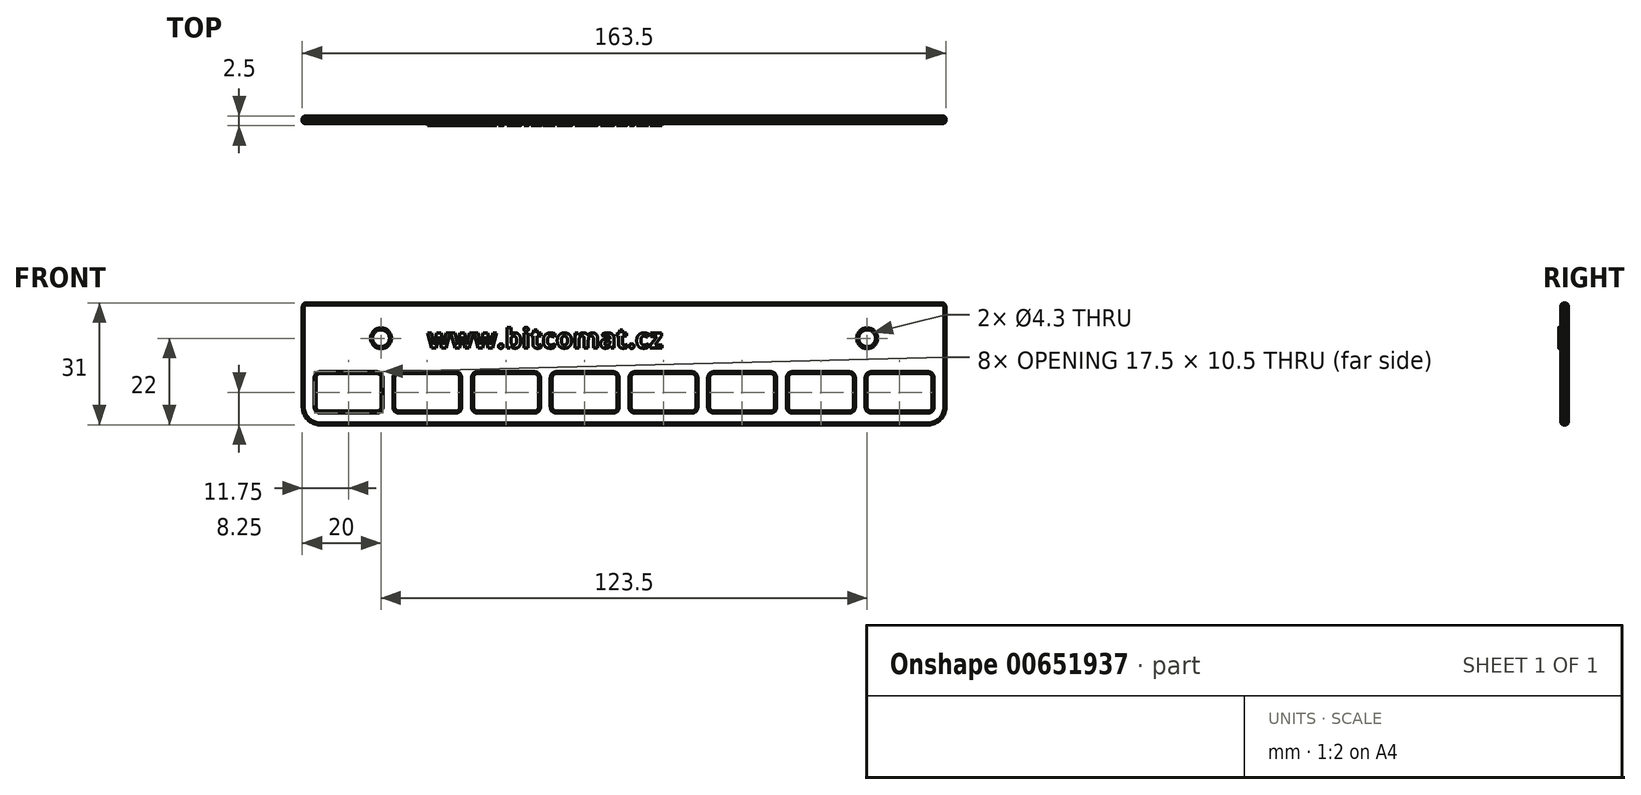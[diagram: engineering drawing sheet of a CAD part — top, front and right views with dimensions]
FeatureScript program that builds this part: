
annotation { "Feature Type Name" : "Feature", "Feature Type Description" : "" }
export const myFeature = defineFeature(function(context is Context, id is Id, definition is map)
    precondition{}
    {
        {
            var Q0;
            Q0=qCreatedBy(makeId("Front.planeOp"),FACE);
            var sketch = newSketch(context, id + "F0", { "sketchPlane" : qUnion([Q0])});
            skLineSegment(sketch, "E0", {"start": v(0, 0) * mm, "end": v(0, 31) * mm});
            skLineSegment(sketch, "E1", {"start": v(0, 31) * mm, "end": v(163.5, 31) * mm});
            skLineSegment(sketch, "E2", {"start": v(163.5, 31) * mm, "end": v(163.5, 0) * mm});
            skCircle(sketch, "E3", {"center": v(20, 22) * mm, "radius": 2.15 * mm});
            skCircle(sketch, "E4", {"center": v(143.5, 22) * mm, "radius": 2.15 * mm});
            skLineSegment(sketch, "E5", {"start": v(0, 0) * mm, "end": v(163.5, 0) * mm});
            skLineSegment(sketch, "E6.bottom", {"start": v(3.5, 13) * mm, "end": v(20, 13) * mm});
            skLineSegment(sketch, "E6.top", {"start": v(3.5, 3.5) * mm, "end": v(20, 3.5) * mm});
            skLineSegment(sketch, "E6.left", {"start": v(3.5, 13) * mm, "end": v(3.5, 3.5) * mm});
            skLineSegment(sketch, "E6.right", {"start": v(20, 13) * mm, "end": v(20, 3.5) * mm});
            skLineSegment(sketch, "E7.bottom", {"start": v(23.5, 13) * mm, "end": v(40, 13) * mm});
            skLineSegment(sketch, "E7.top", {"start": v(23.5, 3.5) * mm, "end": v(40, 3.5) * mm});
            skLineSegment(sketch, "E7.left", {"start": v(23.5, 13) * mm, "end": v(23.5, 3.5) * mm});
            skLineSegment(sketch, "E7.right", {"start": v(40, 13) * mm, "end": v(40, 3.5) * mm});
            skLineSegment(sketch, "E8.bottom", {"start": v(43.5, 13) * mm, "end": v(60, 13) * mm});
            skLineSegment(sketch, "E8.top", {"start": v(43.5, 3.5) * mm, "end": v(60, 3.5) * mm});
            skLineSegment(sketch, "E8.left", {"start": v(43.5, 13) * mm, "end": v(43.5, 3.5) * mm});
            skLineSegment(sketch, "E8.right", {"start": v(60, 13) * mm, "end": v(60, 3.5) * mm});
            skLineSegment(sketch, "E9.bottom", {"start": v(63.5, 13) * mm, "end": v(80, 13) * mm});
            skLineSegment(sketch, "E9.top", {"start": v(63.5, 3.5) * mm, "end": v(80, 3.5) * mm});
            skLineSegment(sketch, "E9.left", {"start": v(63.5, 13) * mm, "end": v(63.5, 3.5) * mm});
            skLineSegment(sketch, "E9.right", {"start": v(80, 13) * mm, "end": v(80, 3.5) * mm});
            skLineSegment(sketch, "E10.bottom", {"start": v(83.5, 13) * mm, "end": v(100, 13) * mm});
            skLineSegment(sketch, "E10.top", {"start": v(83.5, 3.5) * mm, "end": v(100, 3.5) * mm});
            skLineSegment(sketch, "E10.left", {"start": v(83.5, 13) * mm, "end": v(83.5, 3.5) * mm});
            skLineSegment(sketch, "E10.right", {"start": v(100, 13) * mm, "end": v(100, 3.5) * mm});
            skLineSegment(sketch, "E11.bottom", {"start": v(103.5, 13) * mm, "end": v(120, 13) * mm});
            skLineSegment(sketch, "E11.top", {"start": v(103.5, 3.5) * mm, "end": v(120, 3.5) * mm});
            skLineSegment(sketch, "E11.left", {"start": v(103.5, 13) * mm, "end": v(103.5, 3.5) * mm});
            skLineSegment(sketch, "E11.right", {"start": v(120, 13) * mm, "end": v(120, 3.5) * mm});
            skLineSegment(sketch, "E12.bottom", {"start": v(123.5, 13) * mm, "end": v(140, 13) * mm});
            skLineSegment(sketch, "E12.top", {"start": v(123.5, 3.5) * mm, "end": v(140, 3.5) * mm});
            skLineSegment(sketch, "E12.left", {"start": v(123.5, 13) * mm, "end": v(123.5, 3.5) * mm});
            skLineSegment(sketch, "E12.right", {"start": v(140, 13) * mm, "end": v(140, 3.5) * mm});
            skLineSegment(sketch, "E13.bottom", {"start": v(143.5, 13) * mm, "end": v(160, 13) * mm});
            skLineSegment(sketch, "E13.top", {"start": v(143.5, 3.5) * mm, "end": v(160, 3.5) * mm});
            skLineSegment(sketch, "E13.left", {"start": v(143.5, 13) * mm, "end": v(143.5, 3.5) * mm});
            skLineSegment(sketch, "E13.right", {"start": v(160, 13) * mm, "end": v(160, 3.5) * mm});
            skSolve(sketch);
        }
        {
            var Q0;
            Q0 = qSketchRegion(id + "F0", true);
            extrude(context, id + "F1", {"entities" : qUnion([Q0]), "depth" : 2 * mm, "offsetDistance" : 25 * mm});
        }
        {
            var Q0;
            Q0=makeQuery(id+"F1.opExtrude","SWEPT_EDGE",EDGE,{"disambiguationData":[OSD([sQuery(id+"F0.wireOp",EDGE,"8d9dad82-93ce-4f2d-81da-381c7b047625.trimOffspring"),sQuery(id+"F0.wireOp",EDGE,"Q4MqpzYb-z3Ok-xj9e-ZRvY-jZGfUojLIxkK")])]});
            var Q1;
            Q1=makeQuery(id+"F1.opExtrude","SWEPT_EDGE",EDGE,{"disambiguationData":[OSD([sQuery(id+"F0.wireOp",EDGE,"314859cf-d446-4f25-8f78-4489ed11554f.trimOffspring"),sQuery(id+"F0.wireOp",EDGE,"7d0YZfYc-MtNi-HNez-lG2K-TYVgYgpoHqIJ")])]});
            var Q2;
            Q2=makeQuery(id+"F1.opExtrude","SWEPT_EDGE",EDGE,{"disambiguationData":[OSD([sQuery(id+"F0.wireOp",EDGE,"4a782518-a8ca-412a-b276-fc9fadfd2a7f.trimOffspring"),sQuery(id+"F0.wireOp",EDGE,"5vtNxTYR-MAFZ-9926-d2hc-BvAu6AeZHcsb")])]});
            var Q3;
            Q3=makeQuery(id+"F1.opExtrude","SWEPT_EDGE",EDGE,{"disambiguationData":[OSD([sQuery(id+"F0.wireOp",EDGE,"aee5cead-98e0-4757-9163-f8d7b24aee3c.trimOffspring"),sQuery(id+"F0.wireOp",EDGE,"1HIB1zMs-rl4G-Qikl-t2Sc-eNzFZ2GBNpQB")])]});
            var Q4;
            Q4=makeQuery(id+"F1.opExtrude","SWEPT_EDGE",EDGE,{"disambiguationData":[OSD([sQuery(id+"F0.wireOp",EDGE,"952a6334-aa4c-4368-9368-879805710147.trimOffspring"),sQuery(id+"F0.wireOp",EDGE,"39W3pprf-JPW6-z08R-VL7n-OxTiLGvcOl4Z")])]});
            var Q5;
            Q5=makeQuery(id+"F1.opExtrude","SWEPT_EDGE",EDGE,{"disambiguationData":[OSD([sQuery(id+"F0.wireOp",EDGE,"TwgcRK7u-zNJq-IuH6-kE6Y-Pdj6bc34kcyJ"),sQuery(id+"F0.wireOp",EDGE,"NbZKl04f-24VF-Ro1G-Pxu3-JmUhMLliUNzg")])]});
            var Q6;
            Q6=makeQuery(id+"F1.opExtrude","SWEPT_EDGE",EDGE,{"disambiguationData":[OSD([sQuery(id+"F0.wireOp",EDGE,"8d9dad82-93ce-4f2d-81da-381c7b047625.trimOffspring"),sQuery(id+"F0.wireOp",EDGE,"SUHKJSzE-OJzO-pzQp-ywUD-TkapwmwD6V0m")])]});
            var Q7;
            Q7=makeQuery(id+"F1.opExtrude","SWEPT_EDGE",EDGE,{"disambiguationData":[OSD([sQuery(id+"F0.wireOp",EDGE,"7137db87-9400-4fe6-be01-630d94328871.trimOffspring"),sQuery(id+"F0.wireOp",EDGE,"MW19rWYv-jTzx-EUmW-Wu64-N2ipS1HRE4QS")])]});
            var Q8;
            Q8=makeQuery(id+"F1.opExtrude","SWEPT_EDGE",EDGE,{"disambiguationData":[OSD([sQuery(id+"F0.wireOp",EDGE,"314859cf-d446-4f25-8f78-4489ed11554f.trimOffspring"),sQuery(id+"F0.wireOp",EDGE,"OjDirCAP-vRV8-dHmh-1vQw-u1C2cGEMCSFC")])]});
            var Q9;
            Q9=makeQuery(id+"F1.opExtrude","SWEPT_EDGE",EDGE,{"disambiguationData":[OSD([sQuery(id+"F0.wireOp",EDGE,"4a782518-a8ca-412a-b276-fc9fadfd2a7f.trimOffspring"),sQuery(id+"F0.wireOp",EDGE,"MDnvUn5u-0YRr-R42K-GIOI-WnT9jtSQHMXQ")])]});
            var Q10;
            Q10=makeQuery(id+"F1.opExtrude","SWEPT_EDGE",EDGE,{"disambiguationData":[OSD([sQuery(id+"F0.wireOp",EDGE,"aee5cead-98e0-4757-9163-f8d7b24aee3c.trimOffspring"),sQuery(id+"F0.wireOp",EDGE,"P9qTeayO-fJTB-ogTq-NOMs-bO8yJh6IIpOu")])]});
            var Q11;
            Q11=makeQuery(id+"F1.opExtrude","SWEPT_EDGE",EDGE,{"disambiguationData":[OSD([sQuery(id+"F0.wireOp",EDGE,"E0"),sQuery(id+"F0.wireOp",EDGE,"E1")])]});
            var Q12;
            Q12=makeQuery(id+"F1.opExtrude","SWEPT_EDGE",EDGE,{"disambiguationData":[OSD([sQuery(id+"F0.wireOp",EDGE,"E1"),sQuery(id+"F0.wireOp",EDGE,"E2")])]});
            var Q13;
            Q13=makeQuery(id+"F1.opExtrude","SWEPT_EDGE",EDGE,{"disambiguationData":[OSD([sQuery(id+"F0.wireOp",EDGE,"952a6334-aa4c-4368-9368-879805710147.trimOffspring"),sQuery(id+"F0.wireOp",EDGE,"CVMrosdh-o8LT-Kh2A-sdVF-YHnpHe9g5ULG")])]});
            fillet(context, id + "F2", {"entities" : qUnion([Q0, Q1, Q2, Q3, Q4, Q5, Q6, Q7, Q8, Q9, Q10, Q11, Q12, Q13]), "radius" : 1 * mm, "tangentPropagation" : true, "allowEdgeOverflow" : false});
        }
        {
            var Q0;
            Q0=makeQuery(id+"F1.opExtrude","SWEPT_EDGE",EDGE,{"disambiguationData":[OSD([sQuery(id+"F0.wireOp",EDGE,"hVktsJ5d-FybM-sNTf-hAeP-5I45lPSxXoCe"),sQuery(id+"F0.wireOp",EDGE,"Q4MqpzYb-z3Ok-xj9e-ZRvY-jZGfUojLIxkK")])]});
            var Q1;
            Q1=makeQuery(id+"F1.opExtrude","SWEPT_EDGE",EDGE,{"disambiguationData":[OSD([sQuery(id+"F0.wireOp",EDGE,"JEd7AicR-trPV-dsle-exch-AMzUto0O4eAY"),sQuery(id+"F0.wireOp",EDGE,"7d0YZfYc-MtNi-HNez-lG2K-TYVgYgpoHqIJ")])]});
            var Q2;
            Q2=makeQuery(id+"F1.opExtrude","SWEPT_EDGE",EDGE,{"disambiguationData":[OSD([sQuery(id+"F0.wireOp",EDGE,"pn5ojUSX-ob2q-A8bu-eBAn-f9iVDgr16dR8"),sQuery(id+"F0.wireOp",EDGE,"5vtNxTYR-MAFZ-9926-d2hc-BvAu6AeZHcsb")])]});
            var Q3;
            Q3=makeQuery(id+"F1.opExtrude","SWEPT_EDGE",EDGE,{"disambiguationData":[OSD([sQuery(id+"F0.wireOp",EDGE,"OjDirCAP-vRV8-dHmh-1vQw-u1C2cGEMCSFC"),sQuery(id+"F0.wireOp",EDGE,"pn5ojUSX-ob2q-A8bu-eBAn-f9iVDgr16dR8")])]});
            var Q4;
            Q4=makeQuery(id+"F1.opExtrude","SWEPT_EDGE",EDGE,{"disambiguationData":[OSD([sQuery(id+"F0.wireOp",EDGE,"SUHKJSzE-OJzO-pzQp-ywUD-TkapwmwD6V0m"),sQuery(id+"F0.wireOp",EDGE,"JEd7AicR-trPV-dsle-exch-AMzUto0O4eAY")])]});
            var Q5;
            Q5=makeQuery(id+"F1.opExtrude","SWEPT_EDGE",EDGE,{"disambiguationData":[OSD([sQuery(id+"F0.wireOp",EDGE,"MDnvUn5u-0YRr-R42K-GIOI-WnT9jtSQHMXQ"),sQuery(id+"F0.wireOp",EDGE,"S5mCw68c-sqde-8qUc-JXXg-RKrNQSxQ3Wiu")])]});
            var Q6;
            Q6=makeQuery(id+"F1.opExtrude","SWEPT_EDGE",EDGE,{"disambiguationData":[OSD([sQuery(id+"F0.wireOp",EDGE,"P9qTeayO-fJTB-ogTq-NOMs-bO8yJh6IIpOu"),sQuery(id+"F0.wireOp",EDGE,"FKDOqHEf-IVW9-28Ru-xmGw-znab7f26yI2c")])]});
            var Q7;
            Q7=makeQuery(id+"F1.opExtrude","SWEPT_EDGE",EDGE,{"disambiguationData":[OSD([sQuery(id+"F0.wireOp",EDGE,"S5mCw68c-sqde-8qUc-JXXg-RKrNQSxQ3Wiu"),sQuery(id+"F0.wireOp",EDGE,"1HIB1zMs-rl4G-Qikl-t2Sc-eNzFZ2GBNpQB")])]});
            var Q8;
            Q8=makeQuery(id+"F1.opExtrude","SWEPT_EDGE",EDGE,{"disambiguationData":[OSD([sQuery(id+"F0.wireOp",EDGE,"FKDOqHEf-IVW9-28Ru-xmGw-znab7f26yI2c"),sQuery(id+"F0.wireOp",EDGE,"39W3pprf-JPW6-z08R-VL7n-OxTiLGvcOl4Z")])]});
            var Q9;
            Q9=makeQuery(id+"F1.opExtrude","SWEPT_EDGE",EDGE,{"disambiguationData":[OSD([sQuery(id+"F0.wireOp",EDGE,"v1fHItDr-QFj1-3yH0-OkLM-ghUJiiQzrCXv"),sQuery(id+"F0.wireOp",EDGE,"NbZKl04f-24VF-Ro1G-Pxu3-JmUhMLliUNzg")])]});
            var Q10;
            Q10=makeQuery(id+"F1.opExtrude","SWEPT_EDGE",EDGE,{"disambiguationData":[OSD([sQuery(id+"F0.wireOp",EDGE,"CVMrosdh-o8LT-Kh2A-sdVF-YHnpHe9g5ULG"),sQuery(id+"F0.wireOp",EDGE,"v1fHItDr-QFj1-3yH0-OkLM-ghUJiiQzrCXv")])]});
            var Q11;
            Q11=makeQuery(id+"F1.opExtrude","SWEPT_EDGE",EDGE,{"disambiguationData":[OSD([sQuery(id+"F0.wireOp",EDGE,"E2"),sQuery(id+"F0.wireOp",EDGE,"TwgcRK7u-zNJq-IuH6-kE6Y-Pdj6bc34kcyJ")])]});
            var Q12;
            Q12=makeQuery(id+"F1.opExtrude","SWEPT_EDGE",EDGE,{"disambiguationData":[OSD([sQuery(id+"F0.wireOp",EDGE,"E0"),sQuery(id+"F0.wireOp",EDGE,"7137db87-9400-4fe6-be01-630d94328871.trimOffspring")])]});
            var Q13;
            Q13=makeQuery(id+"F1.opExtrude","SWEPT_EDGE",EDGE,{"disambiguationData":[OSD([sQuery(id+"F0.wireOp",EDGE,"MW19rWYv-jTzx-EUmW-Wu64-N2ipS1HRE4QS"),sQuery(id+"F0.wireOp",EDGE,"hVktsJ5d-FybM-sNTf-hAeP-5I45lPSxXoCe")])]});
            fillet(context, id + "F3", {"entities" : qUnion([Q0, Q1, Q2, Q3, Q4, Q5, Q6, Q7, Q8, Q9, Q10, Q11, Q12, Q13]), "radius" : 4.5 * mm, "tangentPropagation" : true, "allowEdgeOverflow" : false});
        }
        {
            var Q0;
            Q0=makeQuery(id+"F1.opExtrude","SWEPT_EDGE",EDGE,{"disambiguationData":[OSD([sQuery(id+"F0.wireOp",EDGE,"E6.bottom"),sQuery(id+"F0.wireOp",EDGE,"E6.left")])]});
            var Q1;
            Q1=makeQuery(id+"F1.opExtrude","SWEPT_EDGE",EDGE,{"disambiguationData":[OSD([sQuery(id+"F0.wireOp",EDGE,"E7.bottom"),sQuery(id+"F0.wireOp",EDGE,"E7.left")])]});
            var Q2;
            Q2=makeQuery(id+"F1.opExtrude","SWEPT_EDGE",EDGE,{"disambiguationData":[OSD([sQuery(id+"F0.wireOp",EDGE,"E8.bottom"),sQuery(id+"F0.wireOp",EDGE,"E8.left")])]});
            var Q3;
            Q3=makeQuery(id+"F1.opExtrude","SWEPT_EDGE",EDGE,{"disambiguationData":[OSD([sQuery(id+"F0.wireOp",EDGE,"E9.bottom"),sQuery(id+"F0.wireOp",EDGE,"E9.left")])]});
            var Q4;
            Q4=makeQuery(id+"F1.opExtrude","SWEPT_EDGE",EDGE,{"disambiguationData":[OSD([sQuery(id+"F0.wireOp",EDGE,"E10.bottom"),sQuery(id+"F0.wireOp",EDGE,"E10.left")])]});
            var Q5;
            Q5=makeQuery(id+"F1.opExtrude","SWEPT_EDGE",EDGE,{"disambiguationData":[OSD([sQuery(id+"F0.wireOp",EDGE,"E11.bottom"),sQuery(id+"F0.wireOp",EDGE,"E11.left")])]});
            var Q6;
            Q6=makeQuery(id+"F1.opExtrude","SWEPT_EDGE",EDGE,{"disambiguationData":[OSD([sQuery(id+"F0.wireOp",EDGE,"E11.bottom"),sQuery(id+"F0.wireOp",EDGE,"E11.right")])]});
            var Q7;
            Q7=makeQuery(id+"F1.opExtrude","SWEPT_EDGE",EDGE,{"disambiguationData":[OSD([sQuery(id+"F0.wireOp",EDGE,"E10.bottom"),sQuery(id+"F0.wireOp",EDGE,"E10.right")])]});
            var Q8;
            Q8=makeQuery(id+"F1.opExtrude","SWEPT_EDGE",EDGE,{"disambiguationData":[OSD([sQuery(id+"F0.wireOp",EDGE,"E9.bottom"),sQuery(id+"F0.wireOp",EDGE,"E9.right")])]});
            var Q9;
            Q9=makeQuery(id+"F1.opExtrude","SWEPT_EDGE",EDGE,{"disambiguationData":[OSD([sQuery(id+"F0.wireOp",EDGE,"E8.bottom"),sQuery(id+"F0.wireOp",EDGE,"E8.right")])]});
            var Q10;
            Q10=makeQuery(id+"F1.opExtrude","SWEPT_EDGE",EDGE,{"disambiguationData":[OSD([sQuery(id+"F0.wireOp",EDGE,"E7.bottom"),sQuery(id+"F0.wireOp",EDGE,"E7.right")])]});
            var Q11;
            Q11=makeQuery(id+"F1.opExtrude","SWEPT_EDGE",EDGE,{"disambiguationData":[OSD([sQuery(id+"F0.wireOp",EDGE,"E6.bottom"),sQuery(id+"F0.wireOp",EDGE,"E6.right")])]});
            var Q12;
            Q12=makeQuery(id+"F1.opExtrude","SWEPT_EDGE",EDGE,{"disambiguationData":[OSD([sQuery(id+"F0.wireOp",EDGE,"E6.top"),sQuery(id+"F0.wireOp",EDGE,"E6.left")])]});
            var Q13;
            Q13=makeQuery(id+"F1.opExtrude","SWEPT_EDGE",EDGE,{"disambiguationData":[OSD([sQuery(id+"F0.wireOp",EDGE,"E7.top"),sQuery(id+"F0.wireOp",EDGE,"E7.left")])]});
            var Q14;
            Q14=makeQuery(id+"F1.opExtrude","SWEPT_EDGE",EDGE,{"disambiguationData":[OSD([sQuery(id+"F0.wireOp",EDGE,"E8.top"),sQuery(id+"F0.wireOp",EDGE,"E8.left")])]});
            var Q15;
            Q15=makeQuery(id+"F1.opExtrude","SWEPT_EDGE",EDGE,{"disambiguationData":[OSD([sQuery(id+"F0.wireOp",EDGE,"E9.top"),sQuery(id+"F0.wireOp",EDGE,"E9.left")])]});
            var Q16;
            Q16=makeQuery(id+"F1.opExtrude","SWEPT_EDGE",EDGE,{"disambiguationData":[OSD([sQuery(id+"F0.wireOp",EDGE,"E10.top"),sQuery(id+"F0.wireOp",EDGE,"E10.left")])]});
            var Q17;
            Q17=makeQuery(id+"F1.opExtrude","SWEPT_EDGE",EDGE,{"disambiguationData":[OSD([sQuery(id+"F0.wireOp",EDGE,"E11.top"),sQuery(id+"F0.wireOp",EDGE,"E11.left")])]});
            var Q18;
            Q18=makeQuery(id+"F1.opExtrude","SWEPT_EDGE",EDGE,{"disambiguationData":[OSD([sQuery(id+"F0.wireOp",EDGE,"E11.top"),sQuery(id+"F0.wireOp",EDGE,"E11.right")])]});
            var Q19;
            Q19=makeQuery(id+"F1.opExtrude","SWEPT_EDGE",EDGE,{"disambiguationData":[OSD([sQuery(id+"F0.wireOp",EDGE,"E10.top"),sQuery(id+"F0.wireOp",EDGE,"E10.right")])]});
            var Q20;
            Q20=makeQuery(id+"F1.opExtrude","SWEPT_EDGE",EDGE,{"disambiguationData":[OSD([sQuery(id+"F0.wireOp",EDGE,"E9.top"),sQuery(id+"F0.wireOp",EDGE,"E9.right")])]});
            var Q21;
            Q21=makeQuery(id+"F1.opExtrude","SWEPT_EDGE",EDGE,{"disambiguationData":[OSD([sQuery(id+"F0.wireOp",EDGE,"E8.top"),sQuery(id+"F0.wireOp",EDGE,"E8.right")])]});
            var Q22;
            Q22=makeQuery(id+"F1.opExtrude","SWEPT_EDGE",EDGE,{"disambiguationData":[OSD([sQuery(id+"F0.wireOp",EDGE,"E7.top"),sQuery(id+"F0.wireOp",EDGE,"E7.right")])]});
            var Q23;
            Q23=makeQuery(id+"F1.opExtrude","SWEPT_EDGE",EDGE,{"disambiguationData":[OSD([sQuery(id+"F0.wireOp",EDGE,"E6.top"),sQuery(id+"F0.wireOp",EDGE,"E6.right")])]});
            var Q24;
            Q24=makeQuery(id+"F1.opExtrude","SWEPT_EDGE",EDGE,{"disambiguationData":[OSD([sQuery(id+"F0.wireOp",EDGE,"E12.bottom"),sQuery(id+"F0.wireOp",EDGE,"E12.left")])]});
            var Q25;
            Q25=makeQuery(id+"F1.opExtrude","SWEPT_EDGE",EDGE,{"disambiguationData":[OSD([sQuery(id+"F0.wireOp",EDGE,"E12.bottom"),sQuery(id+"F0.wireOp",EDGE,"E12.right")])]});
            var Q26;
            Q26=makeQuery(id+"F1.opExtrude","SWEPT_EDGE",EDGE,{"disambiguationData":[OSD([sQuery(id+"F0.wireOp",EDGE,"E13.bottom"),sQuery(id+"F0.wireOp",EDGE,"E13.right")])]});
            var Q27;
            Q27=makeQuery(id+"F1.opExtrude","SWEPT_EDGE",EDGE,{"disambiguationData":[OSD([sQuery(id+"F0.wireOp",EDGE,"E13.bottom"),sQuery(id+"F0.wireOp",EDGE,"E13.left")])]});
            var Q28;
            Q28=makeQuery(id+"F1.opExtrude","SWEPT_EDGE",EDGE,{"disambiguationData":[OSD([sQuery(id+"F0.wireOp",EDGE,"E12.top"),sQuery(id+"F0.wireOp",EDGE,"E12.left")])]});
            var Q29;
            Q29=makeQuery(id+"F1.opExtrude","SWEPT_EDGE",EDGE,{"disambiguationData":[OSD([sQuery(id+"F0.wireOp",EDGE,"E13.top"),sQuery(id+"F0.wireOp",EDGE,"E13.left")])]});
            var Q30;
            Q30=makeQuery(id+"F1.opExtrude","SWEPT_EDGE",EDGE,{"disambiguationData":[OSD([sQuery(id+"F0.wireOp",EDGE,"E12.top"),sQuery(id+"F0.wireOp",EDGE,"E12.right")])]});
            var Q31;
            Q31=makeQuery(id+"F1.opExtrude","SWEPT_EDGE",EDGE,{"disambiguationData":[OSD([sQuery(id+"F0.wireOp",EDGE,"E13.top"),sQuery(id+"F0.wireOp",EDGE,"E13.right")])]});
            fillet(context, id + "F4", {"entities" : qUnion([Q0, Q1, Q2, Q3, Q4, Q5, Q6, Q7, Q8, Q9, Q10, Q11, Q12, Q13, Q14, Q15, Q16, Q17, Q18, Q19, Q20, Q21, Q22, Q23, Q24, Q25, Q26, Q27, Q28, Q29, Q30, Q31]), "radius" : 1 * mm, "tangentPropagation" : true, "defaultsChanged" : false, "vertexSettings" : [], "allowEdgeOverflow" : false});
        }
        {
            var Q0;
            Q0=makeQuery(id+"F1.opExtrude","CAP_FACE",FACE,{"disambiguationData":[OSD([sQuery(id+"F0.wireOp",EDGE,"E0"),sQuery(id+"F0.wireOp",EDGE,"E1"),sQuery(id+"F0.wireOp",EDGE,"E2"),sQuery(id+"F0.wireOp",EDGE,"E3"),sQuery(id+"F0.wireOp",EDGE,"E4"),sQuery(id+"F0.wireOp",EDGE,"E5"),sQuery(id+"F0.wireOp",EDGE,"E6.bottom"),sQuery(id+"F0.wireOp",EDGE,"E6.top"),sQuery(id+"F0.wireOp",EDGE,"E6.left"),sQuery(id+"F0.wireOp",EDGE,"E6.right"),sQuery(id+"F0.wireOp",EDGE,"E7.bottom"),sQuery(id+"F0.wireOp",EDGE,"E7.top"),sQuery(id+"F0.wireOp",EDGE,"E7.left"),sQuery(id+"F0.wireOp",EDGE,"E7.right"),sQuery(id+"F0.wireOp",EDGE,"E8.bottom"),sQuery(id+"F0.wireOp",EDGE,"E8.top"),sQuery(id+"F0.wireOp",EDGE,"E8.left"),sQuery(id+"F0.wireOp",EDGE,"E8.right"),sQuery(id+"F0.wireOp",EDGE,"E9.bottom"),sQuery(id+"F0.wireOp",EDGE,"E9.top"),sQuery(id+"F0.wireOp",EDGE,"E9.left"),sQuery(id+"F0.wireOp",EDGE,"E9.right"),sQuery(id+"F0.wireOp",EDGE,"E10.bottom"),sQuery(id+"F0.wireOp",EDGE,"E10.top"),sQuery(id+"F0.wireOp",EDGE,"E10.left"),sQuery(id+"F0.wireOp",EDGE,"E10.right"),sQuery(id+"F0.wireOp",EDGE,"E11.bottom"),sQuery(id+"F0.wireOp",EDGE,"E11.top"),sQuery(id+"F0.wireOp",EDGE,"E11.left"),sQuery(id+"F0.wireOp",EDGE,"E11.right")])],"isStart":false});
            var Q1;
            Q1=makeQuery(id+"F1.opExtrude","CAP_FACE",FACE,{"disambiguationData":[OSD([sQuery(id+"F0.wireOp",EDGE,"E0"),sQuery(id+"F0.wireOp",EDGE,"E1"),sQuery(id+"F0.wireOp",EDGE,"E2"),sQuery(id+"F0.wireOp",EDGE,"E3"),sQuery(id+"F0.wireOp",EDGE,"E4"),sQuery(id+"F0.wireOp",EDGE,"E5"),sQuery(id+"F0.wireOp",EDGE,"E6.bottom"),sQuery(id+"F0.wireOp",EDGE,"E6.top"),sQuery(id+"F0.wireOp",EDGE,"E6.left"),sQuery(id+"F0.wireOp",EDGE,"E6.right"),sQuery(id+"F0.wireOp",EDGE,"E7.bottom"),sQuery(id+"F0.wireOp",EDGE,"E7.top"),sQuery(id+"F0.wireOp",EDGE,"E7.left"),sQuery(id+"F0.wireOp",EDGE,"E7.right"),sQuery(id+"F0.wireOp",EDGE,"E8.bottom"),sQuery(id+"F0.wireOp",EDGE,"E8.top"),sQuery(id+"F0.wireOp",EDGE,"E8.left"),sQuery(id+"F0.wireOp",EDGE,"E8.right"),sQuery(id+"F0.wireOp",EDGE,"E9.bottom"),sQuery(id+"F0.wireOp",EDGE,"E9.top"),sQuery(id+"F0.wireOp",EDGE,"E9.left"),sQuery(id+"F0.wireOp",EDGE,"E9.right"),sQuery(id+"F0.wireOp",EDGE,"E10.bottom"),sQuery(id+"F0.wireOp",EDGE,"E10.top"),sQuery(id+"F0.wireOp",EDGE,"E10.left"),sQuery(id+"F0.wireOp",EDGE,"E10.right"),sQuery(id+"F0.wireOp",EDGE,"E11.bottom"),sQuery(id+"F0.wireOp",EDGE,"E11.top"),sQuery(id+"F0.wireOp",EDGE,"E11.left"),sQuery(id+"F0.wireOp",EDGE,"E11.right")])],"isStart":true});
            chamfer(context, id + "F5", {"entities" : qUnion([Q0, Q1]), "width" : 0.5 * mm, "tangentPropagation" : true});
        }
        {
            var Q0;
            Q0=makeQuery(id+"F1.opExtrude","CAP_FACE",FACE,{"disambiguationData":[OSD([sQuery(id+"F0.wireOp",EDGE,"E0"),sQuery(id+"F0.wireOp",EDGE,"E1"),sQuery(id+"F0.wireOp",EDGE,"E2"),sQuery(id+"F0.wireOp",EDGE,"E3"),sQuery(id+"F0.wireOp",EDGE,"E4"),sQuery(id+"F0.wireOp",EDGE,"E5"),sQuery(id+"F0.wireOp",EDGE,"E6.bottom"),sQuery(id+"F0.wireOp",EDGE,"E6.top"),sQuery(id+"F0.wireOp",EDGE,"E6.left"),sQuery(id+"F0.wireOp",EDGE,"E6.right"),sQuery(id+"F0.wireOp",EDGE,"E7.bottom"),sQuery(id+"F0.wireOp",EDGE,"E7.top"),sQuery(id+"F0.wireOp",EDGE,"E7.left"),sQuery(id+"F0.wireOp",EDGE,"E7.right"),sQuery(id+"F0.wireOp",EDGE,"E8.bottom"),sQuery(id+"F0.wireOp",EDGE,"E8.top"),sQuery(id+"F0.wireOp",EDGE,"E8.left"),sQuery(id+"F0.wireOp",EDGE,"E8.right"),sQuery(id+"F0.wireOp",EDGE,"E9.bottom"),sQuery(id+"F0.wireOp",EDGE,"E9.top"),sQuery(id+"F0.wireOp",EDGE,"E9.left"),sQuery(id+"F0.wireOp",EDGE,"E9.right"),sQuery(id+"F0.wireOp",EDGE,"E10.bottom"),sQuery(id+"F0.wireOp",EDGE,"E10.top"),sQuery(id+"F0.wireOp",EDGE,"E10.left"),sQuery(id+"F0.wireOp",EDGE,"E10.right"),sQuery(id+"F0.wireOp",EDGE,"E11.bottom"),sQuery(id+"F0.wireOp",EDGE,"E11.top"),sQuery(id+"F0.wireOp",EDGE,"E11.left"),sQuery(id+"F0.wireOp",EDGE,"E11.right")])],"isStart":false});
            var sketch = newSketch(context, id + "F6", { "sketchPlane" : qUnion([Q0])});
            skText(sketch, "E14", { "text": "www.bitcomat.cz", "fontName": "OpenSans-Bold.ttf"});
            skPoint(sketch, "E15", {"position": v(51.75, 22) * mm});
            skPoint(sketch, "E16", {"position": v(20, 22) * mm});
            const initialGuessF6  = {"E14": [0.03175, 0.01952, 1, 0, 0.00497]};
            skSetInitialGuess(sketch, initialGuessF6);
            skSolve(sketch);
        }
        {
            var Q0;
            Q0 = qSketchRegion(id + "F6", true);
            extrude(context, id + "F7", {"entities" : qUnion([Q0]), "operationType" : NewBodyOperationType.ADD, "depth" : 0.5 * mm, "offsetDistance" : 25 * mm});
        }
    });
